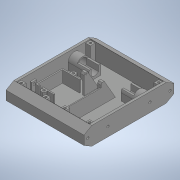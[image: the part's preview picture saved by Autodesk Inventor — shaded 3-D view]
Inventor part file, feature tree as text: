
AUTODESK INVENTOR PART (.ipt)
format: ipt  version: 2020 (Build 240168000, 168)  size: 608,256 bytes
history: native  units: in
note: dims shown in document units (in); Inventor stores cm internally (conversion verified against a paired STEP export)
features: extrude x18, sketch x17, projected_geometry x14, mirror x6, plane x1
ambient origin geometry x8: Origin, YZ Plane, XZ Plane, XY Plane, X Axis, Y Axis, Z Axis, Center Point
bodies: Solid1 (feature_tree)
feature tree (56):
  extrude  "Extrusion1"  Depth=5.9055in
  extrude  "Extrusion2"  TaperAngle=0.0deg  [1 undecoded]
  extrude  "Extrusion3"  Depth=1.063in
  extrude  "Extrusion4"  Depth=0.315in
  extrude  "Extrusion5"  TaperAngle=0.0deg  [1 undecoded]
  extrude  "Extrusion6"  Depth=0.5906in
  mirror  "Mirror1"
  extrude  "Extrusion7"  Depth=0.0787in
  mirror  "Mirror2"
  extrude  "Extrusion8"  Depth=0.6102in
  mirror  "Mirror3"
  plane  "Work Plane1"
  extrude  "Extrusion9"  Depth=0.7874in TaperAngle=0.0deg
  mirror  "Mirror4"
  extrude  "Extrusion10"  Depth=6.063in TaperAngle=0.0deg
  extrude  "Extrusion11"  Depth=0.1575in
  extrude  "Extrusion12"  TaperAngle=0.0deg  [1 undecoded]
  extrude  "Extrusion13"  Depth=0.2756in
  extrude  "Extrusion14"  Depth=0.4331in
  extrude  "Extrusion17"  Depth=2.7559in
  extrude  "Extrusion18"  Depth=0.0413in
  mirror  "Mirror6"
  extrude  "Extrusion19"  TaperAngle=0.0deg  [1 undecoded]
  mirror  "Mirror7"
  extrude  "Extrusion20"  TaperAngle=60.0deg  [1 undecoded]
  sketch  "Sketch1"  dims[d0=1.1811in d1=5.9055in]
  sketch  "Sketch2"  dims[d2=5.1181in d3=0.0in]
  projected_geometry  "Projected Loop1"
  sketch  "Sketch3"  dims[d4=0.1575in d5=1.063in]
  projected_geometry  "Projected Loop2"
  projected_geometry  "Projected Loop3"
  sketch  "Sketch4"  dims[d6=0.0in d8=0.315in]
  projected_geometry  "Projected Loop4"
  sketch  "Sketch6"  dims[d10=0.993in d11=0.0in]
  sketch  "Sketch7"  dims[d12=0.6496in d13=0.5906in]
  sketch  "Sketch9"  dims[d14=1.5748in d15=0.0787in]
  sketch  "Sketch10"  dims[d16=0.5512in d17=0.0in d18=0.6102in]
  sketch  "Sketch12"  dims[d19=0.4803in d20=0.7874in d21=0.0in]
  projected_geometry  "Projected Loop6"
  projected_geometry  "Projected Loop7"
  projected_geometry  "Projected Loop8"
  sketch  "Sketch13"  dims[d22=0.1654in d23=6.063in d24=0.0in]
  sketch  "Sketch14"  dims[d25=0.5114in d26=0.1575in]
  sketch  "Sketch15"  dims[d27=1.5748in d28=0.0in d29=0.0in]
  projected_geometry  "Projected Loop15"
  sketch  "Sketch16"  dims[d30=0.1575in d31=0.2756in]
  projected_geometry  "Projected Loop19"
  projected_geometry  "Projected Loop20"
  projected_geometry  "Projected Loop21"
  projected_geometry  "Projected Loop22"
  projected_geometry  "Projected Loop23"
  projected_geometry  "Projected Loop24"
  sketch  "Sketch20"  dims[d32=0.0in d33=0.4331in]
  sketch  "Sketch21"  dims[d34=0.0827in d38=2.7559in]
  sketch  "Sketch22"  dims[d40=0.0413in d41=0.0909in]
  sketch  "Sketch23"  dims[d42=0.2362in d43=0.0in d44=60.0deg d45=0.0787in d46=0.315in d48=0.993in d49=0.0in d53=0.2756in d54=0.0in d55=0.4724in d56=1.2008in d57=1.6142in d58=1.5945in d59=0.0787in d60=0.0787in d62=0.315in d63=0.7677in d64=0.0in d66=0.1476in d67=0.2756in d68=0.0in d69=0.7874in d70=0.2953in d71=0.1181in d72=0.0in d89=0.0157in d90=0.0157in d91=0.1476in d92=0.1476in d96=0.315in d97=0.1575in d98=0.1181in d99=0.0in d102=0.1772in d104=0.3346in d105=135.0deg d106=0.2362in d107=0.0in d108=0.0394in d109=0.0in d110=0.063in d111=0.0394in d112=0.0in]
note: 5 required parameter values undecoded (feature->parameter linkage not recoverable at this tier; creation-order binding heuristic only, values carry confidence <= 0.55)
